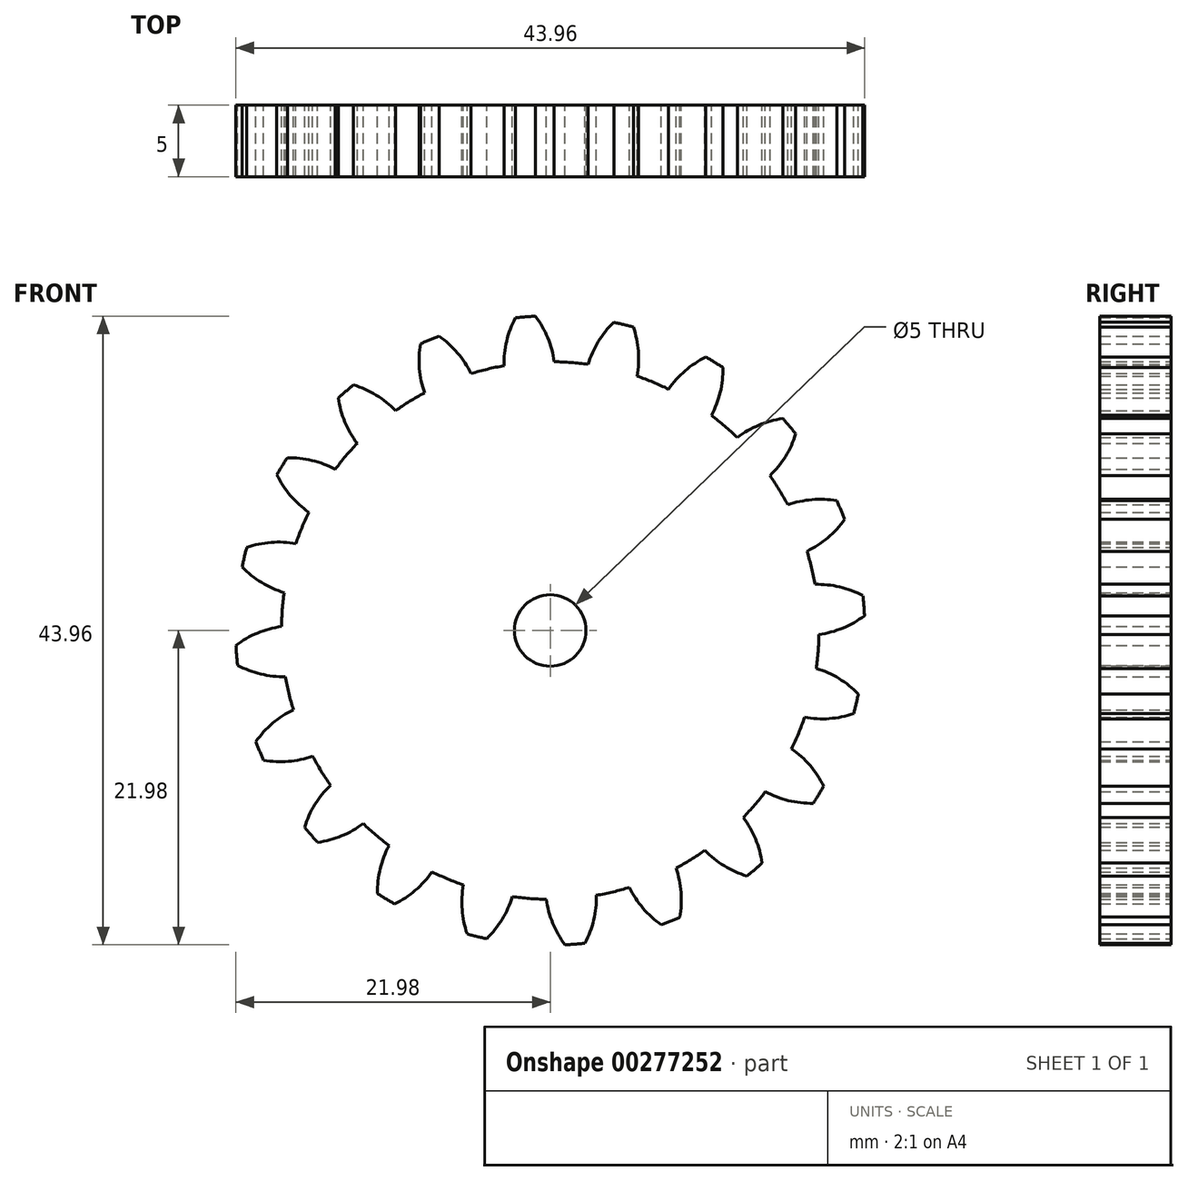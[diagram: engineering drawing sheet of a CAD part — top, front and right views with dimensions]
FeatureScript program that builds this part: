
annotation { "Feature Type Name" : "Feature", "Feature Type Description" : "" }
export const myFeature = defineFeature(function(context is Context, id is Id, definition is map)
    precondition{}
    {
        {
            assignVariable(context, id + "F0", {"name" : "teeth", "anyValue" : 20});
        }
        {
            var Q0;
            Q0=qCreatedBy(makeId("Front.planeOp"),FACE);
            var sketch = newSketch(context, id + "F1", { "sketchPlane" : qUnion([Q0])});
            skCircle(sketch, "E0", {"center": v(0, 0) * mm, "radius": 20 * mm, "construction": true});
            skCircle(sketch, "E1", {"center": v(0, 0) * mm, "radius": 22 * mm, "construction": true});
            skCircle(sketch, "E2", {"center": v(0, 0) * mm, "radius": 18.8 * mm});
            skCircle(sketch, "E3", {"center": v(40, 0) * mm, "radius": 18.8 * mm, "construction": true});
            skLineSegment(sketch, "E4", {"start": v(17.66, 6.43) * mm, "end": v(20, 0) * mm, "construction": true});
            skLineSegment(sketch, "E5", {"start": v(0, 0) * mm, "end": v(20, 0) * mm, "construction": true});
            skLineSegment(sketch, "E6", {"start": v(20, 0) * mm, "end": v(20, 28.46) * mm, "construction": true});
            skLineSegment(sketch, "E7", {"start": v(20, 0) * mm, "end": v(22.34, -6.43) * mm, "construction": true});
            skLineSegment(sketch, "E8", {"start": v(20, 0) * mm, "end": v(40, 0) * mm, "construction": true});
            skLineSegment(sketch, "E9", {"start": v(17.66, 6.43) * mm, "end": v(0, 0) * mm, "construction": true});
            skArc(sketch, "E10", {"start": v(17.66, 6.43) * mm, "mid": v(18.53, 3.13) * mm, "end": v(18.8, -0.28) * mm, "construction": true});
            skArc(sketch, "E11", {"start": v(18.8, -0.28) * mm, "mid": v(18.01, 5.36) * mm, "end": v(15.58, 10.51) * mm, "construction": true});
            skLineSegment(sketch, "E12", {"start": v(15.58, 10.51) * mm, "end": v(0, 0) * mm, "construction": true});
            skLineSegment(sketch, "E13", {"start": v(15.58, 10.51) * mm, "end": v(21.98, 1.03) * mm, "construction": true});
            skLineSegment(sketch, "E14", {"start": v(18.8, -0.28) * mm, "end": v(0, 0) * mm, "construction": true});
            skArc(sketch, "E15", {"start": v(18.8, -0.28) * mm, "mid": v(20.47, 0.17) * mm, "end": v(21.98, 1.03) * mm});
            skLineSegment(sketch, "E16", {"start": v(0, 0) * mm, "end": v(21.93, 1.73) * mm, "construction": true});
            skArc(sketch, "E17.MirrorCS", {"start": v(18.51, 3.23) * mm, "mid": v(20.24, 3.04) * mm, "end": v(21.87, 2.43) * mm});
            skPoint(sketch, "E18", {"position": v(19.75, 3.14) * mm});
            skArc(sketch, "E19", {"start": v(21.98, 1.03) * mm, "mid": v(21.93, 1.73) * mm, "end": v(21.87, 2.43) * mm});
            skPoint(sketch, "E20", {"position": v(18.74, 1.48) * mm});
            skArc(sketch, "E21", {"start": v(18.8, -0.28) * mm, "mid": v(18.74, 1.48) * mm, "end": v(18.51, 3.23) * mm});
            skSolve(sketch);
        }
        {
            var Q0;
            {var subQ0=sQuery(id+"F1.wireOp",EDGE,"E2");var subQ1=makeQuery(id+"F1.imprint","INTERSECT",VERTEX,{"derivedFrom":[subQ0,sQuery(id+"F1.wireOp",EDGE,"E15")]});Q0=makeQuery(id+"F1.imprint","IMPRINT",FACE,{"disambiguationData":[TD([[makeQuery(id+"F1.imprint","IMPRINT",EDGE,{"disambiguationData":[TD([[subQ1,1.0]])],"derivedFrom":subQ0}),1.0]])]});}
            extrude(context, id + "F2", {"entities" : qUnion([Q0]), "depth" : 5 * mm});
        }
        {
            var Q0;
            {var subQ0=sQuery(id+"F1.wireOp",EDGE,"E15");Q0=makeQuery(id+"F1.imprint","IMPRINT",FACE,{"disambiguationData":[TD([[makeQuery(id+"F1.imprint","IMPRINT",EDGE,{"derivedFrom":subQ0}),1.0]])]});}
            extrude(context, id + "F3", {"entities" : qUnion([Q0]), "depth" : 5 * mm});
        }
        {
            var Q0;
            Q0=qCreatedBy(makeId("Right.planeOp"),FACE);
            var sketch = newSketch(context, id + "F4", { "sketchPlane" : qUnion([Q0])});
            skLineSegment(sketch, "E22", {"start": v(0, 0) * mm, "end": v(12.3, 0) * mm});
            skSolve(sketch);
        }
        {
            var Q0;
            Q0=makeQuery(id+"F3.opExtrude","SWEPT_BODY",BODY,{"disambiguationData":[OSD([sQuery(id+"F1.wireOp",EDGE,"E2"),sQuery(id+"F1.wireOp",EDGE,"E15"),sQuery(id+"F1.wireOp",EDGE,"E17.MirrorCS"),sQuery(id+"F1.wireOp",EDGE,"E19")])]});
            var Q1;
            Q1=sQuery(id+"F4.wireOp",EDGE,"E22");
            circularPattern(context, id + "F5", {"operationType" : NewBodyOperationType.ADD, "entities" : qUnion([Q0]), "axis" : qUnion([Q1]), "angle" : (360 / getVariable(context, 'teeth')) * degree, "instanceCount" : getVariable(context, 'teeth')});
        }
        {
            var Q0;
            {var subQ0=sQuery(id+"F1.wireOp",EDGE,"E2");var subQ1=makeQuery(id+"F3.opExtrude","CAP_FACE",FACE,{"disambiguationData":[OSD([subQ0,sQuery(id+"F1.wireOp",EDGE,"E15"),sQuery(id+"F1.wireOp",EDGE,"E17.MirrorCS"),sQuery(id+"F1.wireOp",EDGE,"E19")])],"isStart":false});Q0=makeQuery(id+"F5.boolean.opBoolean","MERGE",FACE,{"derivedFrom":[makeQuery(id+"F2.opExtrude","CAP_FACE",FACE,{"disambiguationData":[OSD([subQ0])],"isStart":false}),subQ1,makeQuery(id+"F5.opPattern","COPY",FACE,{"derivedFrom":subQ1,"instanceName":"1"}),makeQuery(id+"F5.opPattern","COPY",FACE,{"derivedFrom":subQ1,"instanceName":"2"}),makeQuery(id+"F5.opPattern","COPY",FACE,{"derivedFrom":subQ1,"instanceName":"3"}),makeQuery(id+"F5.opPattern","COPY",FACE,{"derivedFrom":subQ1,"instanceName":"4"}),makeQuery(id+"F5.opPattern","COPY",FACE,{"derivedFrom":subQ1,"instanceName":"5"}),makeQuery(id+"F5.opPattern","COPY",FACE,{"derivedFrom":subQ1,"instanceName":"6"}),makeQuery(id+"F5.opPattern","COPY",FACE,{"derivedFrom":subQ1,"instanceName":"7"}),makeQuery(id+"F5.opPattern","COPY",FACE,{"derivedFrom":subQ1,"instanceName":"8"}),makeQuery(id+"F5.opPattern","COPY",FACE,{"derivedFrom":subQ1,"instanceName":"9"}),makeQuery(id+"F5.opPattern","COPY",FACE,{"derivedFrom":subQ1,"instanceName":"10"}),makeQuery(id+"F5.opPattern","COPY",FACE,{"derivedFrom":subQ1,"instanceName":"11"}),makeQuery(id+"F5.opPattern","COPY",FACE,{"derivedFrom":subQ1,"instanceName":"12"}),makeQuery(id+"F5.opPattern","COPY",FACE,{"derivedFrom":subQ1,"instanceName":"13"}),makeQuery(id+"F5.opPattern","COPY",FACE,{"derivedFrom":subQ1,"instanceName":"14"}),makeQuery(id+"F5.opPattern","COPY",FACE,{"derivedFrom":subQ1,"instanceName":"15"}),makeQuery(id+"F5.opPattern","COPY",FACE,{"derivedFrom":subQ1,"instanceName":"16"}),makeQuery(id+"F5.opPattern","COPY",FACE,{"derivedFrom":subQ1,"instanceName":"17"}),makeQuery(id+"F5.opPattern","COPY",FACE,{"derivedFrom":subQ1,"instanceName":"18"}),makeQuery(id+"F5.opPattern","COPY",FACE,{"derivedFrom":subQ1,"instanceName":"19"})]});}
            var sketch = newSketch(context, id + "F6", { "sketchPlane" : qUnion([Q0])});
            skCircle(sketch, "E23", {"center": v(0, 0) * mm, "radius": 3.72 * mm});
            skSolve(sketch);
        }
        {
            var Q0;
            Q0=sQuery(id+"F6.wireOp",VERTEX,"E23.center");
            var Q1;
            Q1=makeQuery(id+"F2.opExtrude","SWEPT_BODY",BODY,{"disambiguationData":[OSD([sQuery(id+"F1.wireOp",EDGE,"E2")])]});
            hole(context, id + "F7", {"style" : HoleStyle.C_SINK, "endStyle" : HoleEndStyle.THROUGH, "holeDiameter" : 5 * mm, "cSinkDiameter" : 5 * mm, "cSinkAngle" : 120 * degree, "tappedDepth" : 12 * mm, "tapClearance" : 3, "locations" : qUnion([Q0]), "scope" : qUnion([Q1])});
        }
    });
